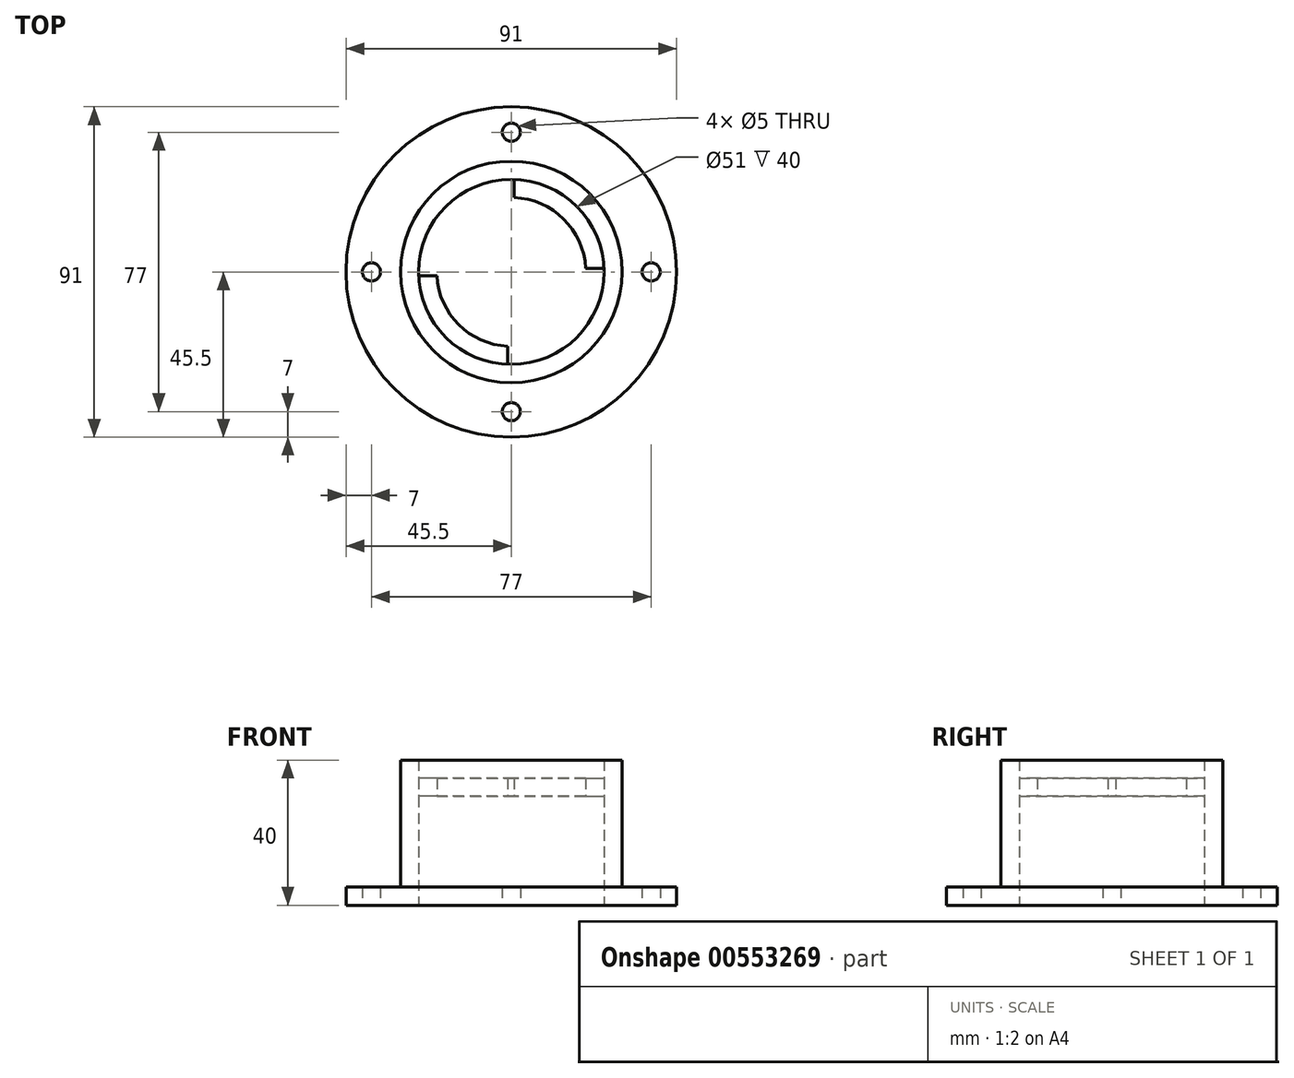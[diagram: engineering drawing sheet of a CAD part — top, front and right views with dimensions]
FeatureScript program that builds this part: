
annotation { "Feature Type Name" : "Feature", "Feature Type Description" : "" }
export const myFeature = defineFeature(function(context is Context, id is Id, definition is map)
    precondition{}
    {
        {
            var Q0;
            Q0=qCreatedBy(makeId("Top.planeOp"),FACE);
            var sketch = newSketch(context, id + "F0", { "sketchPlane" : qUnion([Q0])});
            skCircle(sketch, "E0", {"center": v(0, 0) * mm, "radius": 30.5 * mm});
            skCircle(sketch, "E1", {"center": v(0, 0) * mm, "radius": 45.5 * mm});
            skCircle(sketch, "E2", {"center": v(0, 0) * mm, "radius": 25.5 * mm});
            skPoint(sketch, "E3", {"position": v(-45.5, 0) * mm});
            skPoint(sketch, "E4", {"position": v(0, 45.5) * mm});
            skPoint(sketch, "E5", {"position": v(45.5, 0) * mm});
            skPoint(sketch, "E6", {"position": v(0, -45.5) * mm});
            skPoint(sketch, "E7", {"position": v(0, -38.5) * mm});
            skPoint(sketch, "E8", {"position": v(-38.5, 0) * mm});
            skPoint(sketch, "E9", {"position": v(0, 38.5) * mm});
            skPoint(sketch, "E10", {"position": v(38.5, 0) * mm});
            skArc(sketch, "E11", {"start": v(0.74, 20.49) * mm, "mid": v(14.4, 14.59) * mm, "end": v(20.48, 1) * mm});
            skLineSegment(sketch, "E12", {"start": v(0.74, 20.49) * mm, "end": v(0.74, 25.49) * mm});
            skLineSegment(sketch, "E13", {"start": v(20.48, 1) * mm, "end": v(25.48, 1) * mm});
            skArc(sketch, "E14", {"start": v(-0.95, -20.48) * mm, "mid": v(-14.46, -14.53) * mm, "end": v(-20.47, -1.05) * mm});
            skLineSegment(sketch, "E15", {"start": v(-20.47, -1.05) * mm, "end": v(-25.48, -1.05) * mm});
            skLineSegment(sketch, "E16", {"start": v(-0.95, -20.48) * mm, "end": v(-0.95, -25.48) * mm});
            skSolve(sketch);
        }
        {
            var Q0;
            Q0=qSketchRegion(id+"F0",true);
            extrude(context, id + "F1", {"entities" : qUnion([Q0]), "depth" : 5 * mm, "offsetDistance" : 25 * mm});
        }
        {
            var Q0;
            Q0=makeQuery(id+"F0.imprint","IMPRINT",FACE,{"disambiguationData":[TD([[makeQuery(id+"F0.imprint","IMPRINT",EDGE,{"derivedFrom":sQuery(id+"F0.wireOp",EDGE,"E0")}),1.0]])]});
            extrude(context, id + "F2", {"entities" : qUnion([Q0]), "operationType" : NewBodyOperationType.ADD, "depth" : 40 * mm, "offsetDistance" : 25 * mm});
        }
        {
            var Q0;
            Q0=sQuery(id+"F0.wireOp",VERTEX,"E10");
            var Q1;
            Q1=sQuery(id+"F0.wireOp",VERTEX,"E8");
            var Q2;
            Q2=sQuery(id+"F0.wireOp",VERTEX,"E7");
            var Q3;
            Q3=sQuery(id+"F0.wireOp",VERTEX,"E9");
            var Q4;
            Q4=makeQuery(id+"F1.opExtrude","SWEPT_BODY",BODY,{"disambiguationData":[OSD([sQuery(id+"F0.wireOp",EDGE,"E0"),sQuery(id+"F0.wireOp",EDGE,"E1")])]});
            hole(context, id + "F3", {"style" : HoleStyle.SIMPLE, "endStyle" : HoleEndStyle.BLIND, "oppositeDirection" : true, "holeDiameter" : 5 * mm, "holeDepth" : 12 * mm, "isTappedThrough" : true, "tappedDepth" : 12 * mm, "tapClearance" : 3, "locations" : qUnion([Q0, Q1, Q2, Q3]), "scope" : qUnion([Q4])});
        }
        {
            var Q0;
            Q0=makeQuery(id+"F0.imprint","IMPRINT",FACE,{"disambiguationData":[TD([[makeQuery(id+"F0.imprint","IMPRINT",EDGE,{"derivedFrom":sQuery(id+"F0.wireOp",EDGE,"E11")}),1.0]])]});
            var Q1;
            Q1=makeQuery(id+"F0.imprint","IMPRINT",FACE,{"disambiguationData":[TD([[makeQuery(id+"F0.imprint","IMPRINT",EDGE,{"derivedFrom":sQuery(id+"F0.wireOp",EDGE,"E14")}),1.0]])]});
            extrude(context, id + "F4", {"entities" : qUnion([Q0, Q1]), "operationType" : NewBodyOperationType.ADD, "depth" : 35 * mm, "offsetDistance" : 25 * mm, "hasSecondDirection" : true, "secondDirectionOppositeDirection" : true, "secondDirectionDepth" : -30 * mm});
        }
    });
